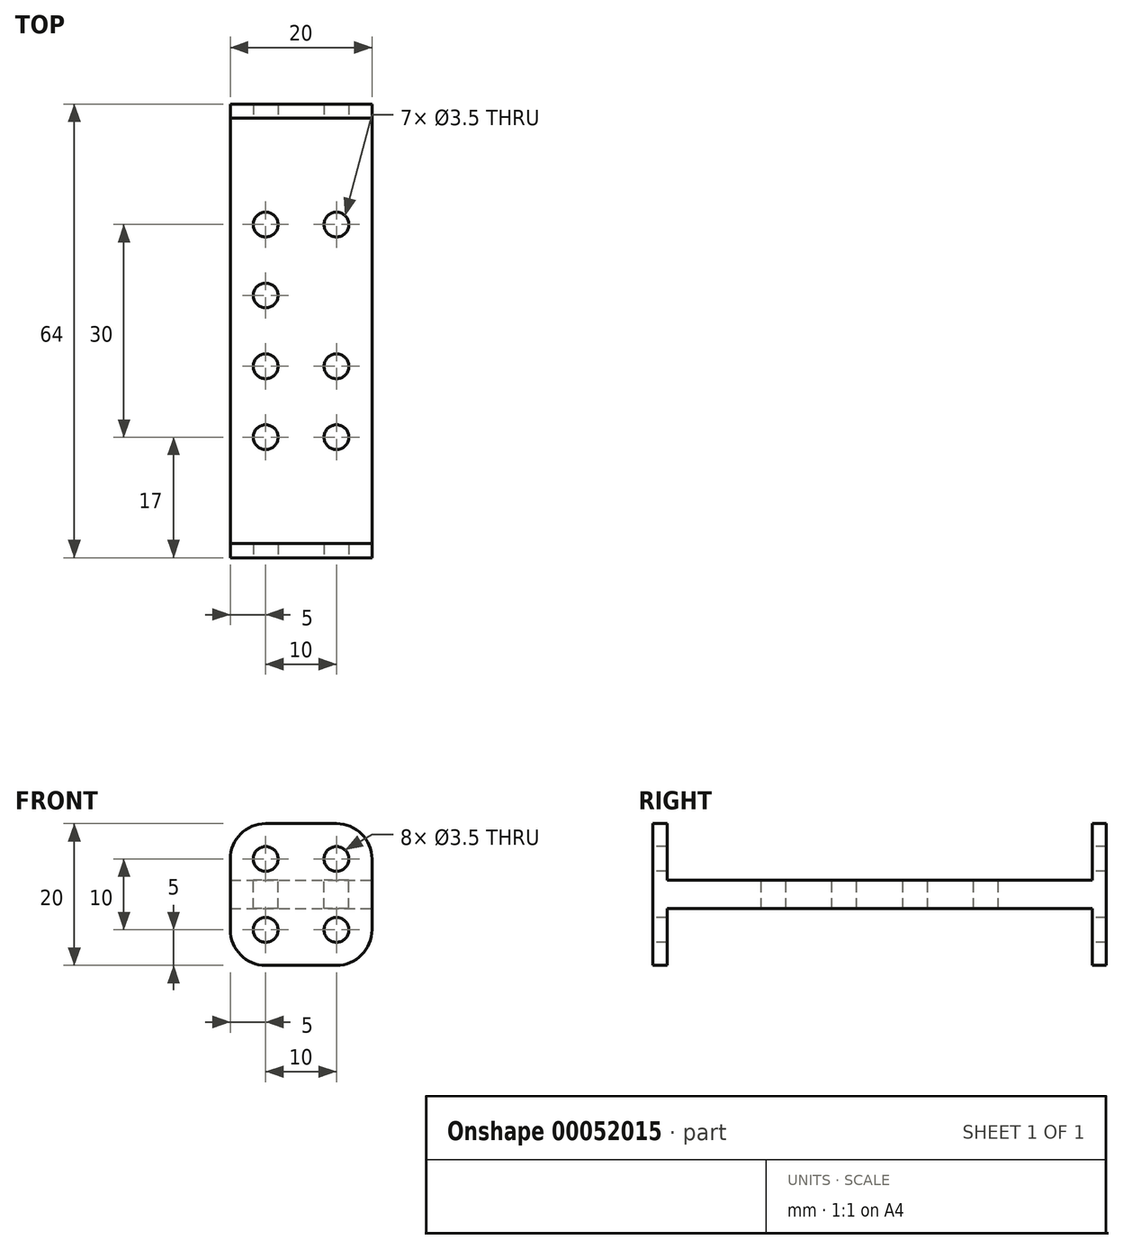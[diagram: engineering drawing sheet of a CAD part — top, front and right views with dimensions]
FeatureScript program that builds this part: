
annotation { "Feature Type Name" : "Feature", "Feature Type Description" : "" }
export const myFeature = defineFeature(function(context is Context, id is Id, definition is map)
    precondition{}
    {
        {
            var Q0;
            Q0=qCreatedBy(makeId("Top.planeOp"),FACE);
            var sketch = newSketch(context, id + "F0", { "sketchPlane" : qUnion([Q0])});
            skLineSegment(sketch, "E0.bottom", {"start": v(-10, 30) * mm, "end": v(10, 30) * mm});
            skLineSegment(sketch, "E0.top", {"start": v(-10, -30) * mm, "end": v(10, -30) * mm});
            skLineSegment(sketch, "E0.left", {"start": v(-10, 30) * mm, "end": v(-10, -30) * mm});
            skLineSegment(sketch, "E0.right", {"start": v(10, 30) * mm, "end": v(10, -30) * mm});
            skLineSegment(sketch, "E1", {"start": v(-10, 30) * mm, "end": v(10, -30) * mm, "construction": true});
            skPoint(sketch, "E2", {"position": v(0, 0) * mm});
            skSolve(sketch);
        }
        {
            var Q0;
            Q0=makeQuery(id+"F0.imprint","IMPRINT",FACE,{"disambiguationData":[TD([[makeQuery(id+"F0.imprint","IMPRINT",EDGE,{"derivedFrom":sQuery(id+"F0.wireOp",EDGE,"E0.bottom")}),-1.0]])]});
            extrude(context, id + "F1", {"entities" : qUnion([Q0]), "endBound" : BoundingType.SYMMETRIC, "depth" : 4 * mm});
        }
        {
            var Q0;
            Q0=makeQuery(id+"F1.opExtrude","SWEPT_FACE",FACE,{"disambiguationData":[OSD([sQuery(id+"F0.wireOp",EDGE,"E0.bottom")])]});
            var sketch = newSketch(context, id + "F2", { "sketchPlane" : qUnion([Q0])});
            skLineSegment(sketch, "E3.bottom", {"start": v(-10, 10) * mm, "end": v(10, 10) * mm});
            skLineSegment(sketch, "E3.top", {"start": v(-10, -10) * mm, "end": v(10, -10) * mm});
            skLineSegment(sketch, "E3.left", {"start": v(-10, 10) * mm, "end": v(-10, -10) * mm});
            skLineSegment(sketch, "E3.right", {"start": v(10, 10) * mm, "end": v(10, -10) * mm});
            skLineSegment(sketch, "E4", {"start": v(-10, 10) * mm, "end": v(10, -10) * mm});
            skPoint(sketch, "E5", {"position": v(0, 0) * mm});
            skSolve(sketch);
        }
        {
            var Q0;
            Q0=makeQuery(id+"F2.imprint","IMPRINT",FACE,{"disambiguationData":[TD([[makeQuery(id+"F2.imprint","IMPRINT",EDGE,{"derivedFrom":sQuery(id+"F2.wireOp",EDGE,"qRdVC1FZ-xQav-RF3d-485T-ApkGFffO4ypK")}),1.0]])]});
            var Q1;
            Q1=makeQuery(id+"F2.imprint","IMPRINT",FACE,{"disambiguationData":[TD([[makeQuery(id+"F2.imprint","IMPRINT",EDGE,{"derivedFrom":sQuery(id+"F2.wireOp",EDGE,"qRdVC1FZ-xQav-RF3d-485T-ApkGFffO4ypK")}),1.0]])]});
            var Q2;
            {var subQ0=sQuery(id+"F0.wireOp",EDGE,"E0.bottom");Q2=makeQuery(id+"F2.imprint","IMPRINT",FACE,{"disambiguationData":[TD([[makeQuery(id+"F2.imprint","IMPRINT",EDGE,{"derivedFrom":makeQuery(id+"F1.opExtrude","CAP_EDGE",EDGE,{"disambiguationData":[OSD([subQ0])],"isStart":true})}),-1.0]])]});}
            var Q3;
            {var subQ0=sQuery(id+"F2.wireOp",EDGE,"E3.bottom");Q3=makeQuery(id+"F2.imprint","IMPRINT",FACE,{"disambiguationData":[TD([[makeQuery(id+"F2.imprint","IMPRINT",EDGE,{"derivedFrom":subQ0}),-1.0]])]});}
            var Q4;
            {var subQ0=sQuery(id+"F2.wireOp",EDGE,"E3.top");Q4=makeQuery(id+"F2.imprint","IMPRINT",FACE,{"disambiguationData":[TD([[makeQuery(id+"F2.imprint","IMPRINT",EDGE,{"derivedFrom":subQ0}),1.0]])]});}
            var Q5;
            {var subQ0=sQuery(id+"F2.wireOp",EDGE,"E3.right");var subQ1=makeQuery(id+"F1.opExtrude","CAP_EDGE",EDGE,{"disambiguationData":[OSD([sQuery(id+"F0.wireOp",EDGE,"E0.bottom")])],"isStart":true});var subQ2=makeQuery(id+"F2.imprint","INTERSECT",VERTEX,{"derivedFrom":[subQ1,subQ0]});Q5=makeQuery(id+"F2.imprint","IMPRINT",FACE,{"disambiguationData":[TD([[makeQuery(id+"F2.imprint","IMPRINT",EDGE,{"disambiguationData":[TD([[subQ2,-1.0]])],"derivedFrom":subQ1}),1.0]])]});}
            var Q6;
            {var subQ0=sQuery(id+"F2.wireOp",EDGE,"E3.left");var subQ1=makeQuery(id+"F1.opExtrude","CAP_EDGE",EDGE,{"disambiguationData":[OSD([sQuery(id+"F0.wireOp",EDGE,"E0.bottom")])],"isStart":false});var subQ2=makeQuery(id+"F2.imprint","INTERSECT",VERTEX,{"derivedFrom":[subQ1,subQ0]});Q6=makeQuery(id+"F2.imprint","IMPRINT",FACE,{"disambiguationData":[TD([[makeQuery(id+"F2.imprint","IMPRINT",EDGE,{"disambiguationData":[TD([[subQ2,1.0]])],"derivedFrom":subQ1}),-1.0]])]});}
            extrude(context, id + "F3", {"entities" : qUnion([Q0, Q1, Q2, Q3, Q4, Q5, Q6]), "operationType" : NewBodyOperationType.ADD, "depth" : 2 * mm});
        }
        {
            var Q0;
            Q0=makeQuery(id+"F1.opExtrude","CAP_FACE",FACE,{"disambiguationData":[OSD([sQuery(id+"F0.wireOp",EDGE,"E0.bottom"),sQuery(id+"F0.wireOp",EDGE,"E0.top"),sQuery(id+"F0.wireOp",EDGE,"E0.left"),sQuery(id+"F0.wireOp",EDGE,"E0.right")])],"isStart":false});
            var sketch = newSketch(context, id + "F4", { "sketchPlane" : qUnion([Q0])});
            skLineSegment(sketch, "E6.bottom", {"start": v(-5, 5) * mm, "end": v(5, 5) * mm});
            skLineSegment(sketch, "E6.top", {"start": v(-5, -5) * mm, "end": v(5, -5) * mm});
            skLineSegment(sketch, "E6.left", {"start": v(-5, 5) * mm, "end": v(-5, -5) * mm});
            skLineSegment(sketch, "E6.right", {"start": v(5, 5) * mm, "end": v(5, -5) * mm});
            skLineSegment(sketch, "E7.top", {"start": v(-5, 15) * mm, "end": v(5, 15) * mm});
            skLineSegment(sketch, "E7.left", {"start": v(-5, 5) * mm, "end": v(-5, 15) * mm});
            skLineSegment(sketch, "E7.right", {"start": v(5, 5) * mm, "end": v(5, 15) * mm});
            skLineSegment(sketch, "E8.bottom", {"start": v(5, 15) * mm, "end": v(-5, 15) * mm});
            skLineSegment(sketch, "E9.top", {"start": v(-5, -15) * mm, "end": v(5, -15) * mm});
            skLineSegment(sketch, "E9.left", {"start": v(-5, -5) * mm, "end": v(-5, -15) * mm});
            skLineSegment(sketch, "E9.right", {"start": v(5, -5) * mm, "end": v(5, -15) * mm});
            skLineSegment(sketch, "E10.bottom", {"start": v(5, -15) * mm, "end": v(-5, -15) * mm});
            skLineSegment(sketch, "E11", {"start": v(-5, 5) * mm, "end": v(5, -5) * mm});
            skPoint(sketch, "E12", {"position": v(0, 0) * mm});
            skSolve(sketch);
        }
        {
            var Q0;
            Q0=sQuery(id+"F4.wireOp",VERTEX,"E8.top.end");
            var Q1;
            Q1=sQuery(id+"F4.wireOp",VERTEX,"E8.left.end");
            var Q2;
            Q2=sQuery(id+"F4.wireOp",VERTEX,"E7.top.end");
            var Q3;
            Q3=sQuery(id+"F4.wireOp",VERTEX,"E8.bottom.end");
            var Q4;
            Q4=sQuery(id+"F4.wireOp",VERTEX,"E6.bottom.start");
            var Q5;
            Q5=sQuery(id+"F4.wireOp",VERTEX,"E6.bottom.end");
            var Q6;
            Q6=sQuery(id+"F4.wireOp",VERTEX,"E9.right.start");
            var Q7;
            Q7=sQuery(id+"F4.wireOp",VERTEX,"E9.left.start");
            var Q8;
            Q8=sQuery(id+"F4.wireOp",VERTEX,"E10.bottom.end");
            var Q9;
            Q9=sQuery(id+"F4.wireOp",VERTEX,"E10.bottom.start");
            var Q10;
            Q10=sQuery(id+"F4.wireOp",VERTEX,"E10.left.end");
            var Q11;
            Q11=sQuery(id+"F4.wireOp",VERTEX,"E10.top.end");
            var Q12;
            Q12=makeQuery(id+"F1.opExtrude","SWEPT_BODY",BODY,{"disambiguationData":[OSD([sQuery(id+"F0.wireOp",EDGE,"E0.bottom"),sQuery(id+"F0.wireOp",EDGE,"E0.top"),sQuery(id+"F0.wireOp",EDGE,"E0.left"),sQuery(id+"F0.wireOp",EDGE,"E0.right")])]});
            hole(context, id + "F5", {"style" : HoleStyle.SIMPLE, "holeDiameter" : 3.5 * mm, "endStyle" : HoleEndStyle.THROUGH, "locations" : qUnion([Q0, Q1, Q2, Q3, Q4, Q5, Q6, Q7, Q8, Q9, Q10, Q11]), "scope" : qUnion([Q12]), "isTappedThrough" : true});
        }
        {
            var Q0;
            Q0=makeQuery(id+"F1.opExtrude","SWEPT_FACE",FACE,{"disambiguationData":[OSD([sQuery(id+"F0.wireOp",EDGE,"E0.top")])]});
            var sketch = newSketch(context, id + "F6", { "sketchPlane" : qUnion([Q0])});
            skLineSegment(sketch, "E13.bottom", {"start": v(-10, 10) * mm, "end": v(10, 10) * mm});
            skLineSegment(sketch, "E13.top", {"start": v(-10, -10) * mm, "end": v(10, -10) * mm});
            skLineSegment(sketch, "E13.left", {"start": v(-10, 10) * mm, "end": v(-10, -10) * mm});
            skLineSegment(sketch, "E13.right", {"start": v(10, 10) * mm, "end": v(10, -10) * mm});
            skSolve(sketch);
        }
        {
            var Q0;
            {var subQ0=sQuery(id+"F6.wireOp",EDGE,"E13.bottom");Q0=makeQuery(id+"F6.imprint","IMPRINT",FACE,{"disambiguationData":[TD([[makeQuery(id+"F6.imprint","IMPRINT",EDGE,{"derivedFrom":subQ0}),-1.0]])]});}
            var Q1;
            {var subQ1=sQuery(id+"F0.wireOp",EDGE,"E0.top");var subQ2=makeQuery(id+"F1.opExtrude","CAP_EDGE",EDGE,{"disambiguationData":[OSD([subQ1])],"isStart":true});Q1=makeQuery(id+"F6.imprint","IMPRINT",FACE,{"disambiguationData":[TD([[makeQuery(id+"F6.imprint","IMPRINT",EDGE,{"derivedFrom":subQ2}),1.0]])]});}
            var Q2;
            {var subQ0=sQuery(id+"F6.wireOp",EDGE,"E13.top");Q2=makeQuery(id+"F6.imprint","IMPRINT",FACE,{"disambiguationData":[TD([[makeQuery(id+"F6.imprint","IMPRINT",EDGE,{"derivedFrom":subQ0}),1.0]])]});}
            extrude(context, id + "F7", {"entities" : qUnion([Q0, Q1, Q2]), "operationType" : NewBodyOperationType.ADD, "depth" : 2 * mm});
        }
        {
            var Q0;
            Q0=makeQuery(id+"F7.opExtrude","CAP_FACE",FACE,{"disambiguationData":[OSD([sQuery(id+"F6.wireOp",EDGE,"E13.bottom"),sQuery(id+"F6.wireOp",EDGE,"E13.top"),sQuery(id+"F6.wireOp",EDGE,"E13.left"),sQuery(id+"F6.wireOp",EDGE,"E13.right")])],"isStart":false});
            var sketch = newSketch(context, id + "F8", { "sketchPlane" : qUnion([Q0])});
            skLineSegment(sketch, "E14.bottom", {"start": v(-5, 5) * mm, "end": v(5, 5) * mm});
            skLineSegment(sketch, "E14.top", {"start": v(-5, -5) * mm, "end": v(5, -5) * mm});
            skLineSegment(sketch, "E14.left", {"start": v(-5, 5) * mm, "end": v(-5, -5) * mm});
            skLineSegment(sketch, "E14.right", {"start": v(5, 5) * mm, "end": v(5, -5) * mm});
            skLineSegment(sketch, "E15", {"start": v(-5, 5) * mm, "end": v(5, -5) * mm});
            skPoint(sketch, "E16", {"position": v(0, 0) * mm});
            skSolve(sketch);
        }
        {
            var Q0;
            Q0=sQuery(id+"F8.wireOp",VERTEX,"E14.bottom.start");
            var Q1;
            Q1=sQuery(id+"F8.wireOp",VERTEX,"E14.bottom.end");
            var Q2;
            Q2=sQuery(id+"F8.wireOp",VERTEX,"E15.end");
            var Q3;
            Q3=sQuery(id+"F8.wireOp",VERTEX,"E14.left.end");
            var Q4;
            Q4=makeQuery(id+"F1.opExtrude","SWEPT_BODY",BODY,{"disambiguationData":[OSD([sQuery(id+"F0.wireOp",EDGE,"E0.bottom"),sQuery(id+"F0.wireOp",EDGE,"E0.top"),sQuery(id+"F0.wireOp",EDGE,"E0.left"),sQuery(id+"F0.wireOp",EDGE,"E0.right")])]});
            hole(context, id + "F9", {"style" : HoleStyle.SIMPLE, "endStyle" : HoleEndStyle.THROUGH, "holeDiameter" : 3.5 * mm, "locations" : qUnion([Q0, Q1, Q2, Q3]), "scope" : qUnion([Q4]), "isTappedThrough" : true});
        }
        {
            var Q0;
            Q0=makeQuery(id+"F7.opExtrude","SWEPT_EDGE",EDGE,{"disambiguationData":[OSD([sQuery(id+"F6.wireOp",EDGE,"E13.bottom"),sQuery(id+"F6.wireOp",EDGE,"E13.right")])]});
            var Q1;
            Q1=makeQuery(id+"F7.opExtrude","SWEPT_EDGE",EDGE,{"disambiguationData":[OSD([sQuery(id+"F6.wireOp",EDGE,"E13.top"),sQuery(id+"F6.wireOp",EDGE,"E13.right")])]});
            var Q2;
            Q2=makeQuery(id+"F3.opExtrude","SWEPT_EDGE",EDGE,{"disambiguationData":[OSD([sQuery(id+"F2.wireOp",EDGE,"E3.bottom"),sQuery(id+"F2.wireOp",EDGE,"E3.left"),sQuery(id+"F2.wireOp",EDGE,"E4")])]});
            var Q3;
            Q3=makeQuery(id+"F3.opExtrude","SWEPT_EDGE",EDGE,{"disambiguationData":[OSD([sQuery(id+"F2.wireOp",EDGE,"E3.top"),sQuery(id+"F2.wireOp",EDGE,"E3.left")])]});
            var Q4;
            Q4=makeQuery(id+"F3.opExtrude","SWEPT_EDGE",EDGE,{"disambiguationData":[OSD([sQuery(id+"F2.wireOp",EDGE,"E3.top"),sQuery(id+"F2.wireOp",EDGE,"E3.right"),sQuery(id+"F2.wireOp",EDGE,"E4")])]});
            var Q5;
            Q5=makeQuery(id+"F3.opExtrude","SWEPT_EDGE",EDGE,{"disambiguationData":[OSD([sQuery(id+"F2.wireOp",EDGE,"E3.bottom"),sQuery(id+"F2.wireOp",EDGE,"E3.right")])]});
            var Q6;
            Q6=makeQuery(id+"F7.opExtrude","SWEPT_EDGE",EDGE,{"disambiguationData":[OSD([sQuery(id+"F6.wireOp",EDGE,"E13.bottom"),sQuery(id+"F6.wireOp",EDGE,"E13.left")])]});
            var Q7;
            Q7=makeQuery(id+"F7.opExtrude","SWEPT_EDGE",EDGE,{"disambiguationData":[OSD([sQuery(id+"F6.wireOp",EDGE,"E13.top"),sQuery(id+"F6.wireOp",EDGE,"E13.left")])]});
            fillet(context, id + "F10", {"entities" : qUnion([Q0, Q1, Q2, Q3, Q4, Q5, Q6, Q7]), "radius" : 5 * mm, "tangentPropagation" : true, "allowEdgeOverflow" : false});
        }
    });
